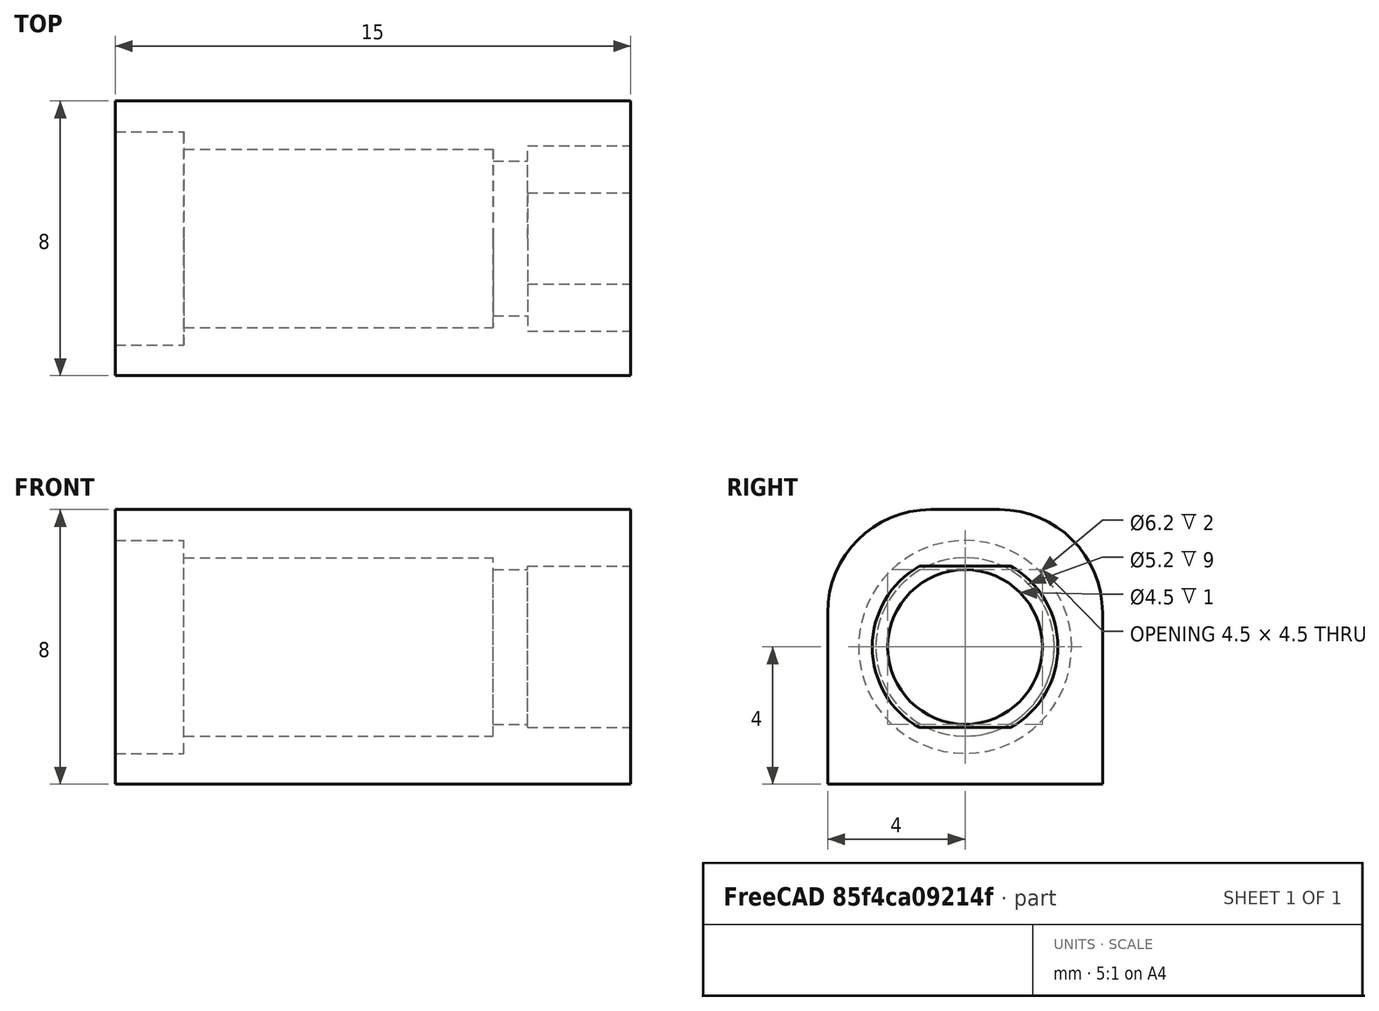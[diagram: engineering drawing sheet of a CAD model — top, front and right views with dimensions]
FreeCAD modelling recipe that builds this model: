
FCSTD DOCUMENT  (FreeCAD 0.14R3700 (Git))
Label: Vactrol_20150326
License: CC-BY 3.0
LicenseURL: http://creativecommons.org/licenses/by/3.0/
objects: Part::Fuse×5, Part::Cylinder×4, Part::Fillet×2, Part::Box×2, Part::Cut×1
note: 14 computed .brp shape members not serialized (recipe doc carries the construction recipe); baked Part::Feature solids carry a one-line shape summary decoded from their .brp

FEATURE [Part::Fillet] Fillet
  Edges = 1 edges r=3: [Edge10]
FEATURE [Part::Fillet] Fillet001  label="housing"
  Base = -> Fillet
  Edges = 1 edges r=3: [Edge13]
  Placement = pos=(0,-4,-4) rot=(0,0,1;0rad)
FEATURE [Part::Cylinder] Cylinder  label="main_bore"
  Angle = 360
  Height = 15
  Placement = pos=(0,0,0) rot=(0,1,0;1.5708rad)
  Radius = 2.25
FEATURE [Part::Cylinder] Cylinder001  label="LED_tip_bore"
  Angle = 360
  Height = 11
  Placement = pos=(0,0,0) rot=(0,1,0;1.5708rad)
  Radius = 2.6
FEATURE [Part::Cylinder] Cylinder002  label="LED_rim_bore"
  Angle = 360
  Height = 2
  Placement = pos=(0,0,0) rot=(0,1,0;1.5708rad)
  Radius = 3.1
FEATURE [Part::Cylinder] Cylinder003  label="LDR_bore"
  Angle = 360
  Height = 3
  Placement = pos=(12,0,0) rot=(0,1,0;1.5708rad)
  Radius = 2.7
FEATURE [Part::Fuse] Fusion  label="LED_bore"
  Base = -> Cylinder001
  Tool = -> Cylinder002
FEATURE [Part::Fuse] Fusion001  label="component_bores"
  Base = -> Cylinder003
  Tool = -> Fusion
FEATURE [Part::Fuse] Fusion002  label="bores"
  Base = -> Cylinder
  Tool = -> Fusion001
FEATURE [Part::Cut] Cut
  Base = -> Fillet001
  Tool = -> Fusion002
FEATURE [Part::Box] Box  label="LDR_guide_bottom"
  Height = 1.65
  Length = 3.5
  Placement = pos=(11.5,-4,-4) rot=(0,0,1;0rad)
  Width = 8
FEATURE [Part::Box] Box001  label="LDR_guide_top"
  Height = 0.45
  Length = 3.5
  Placement = pos=(11.5,-3,2.35) rot=(0,0,1;0rad)
  Width = 6
FEATURE [Part::Fuse] Fusion003  label="LDR_guides"
  Base = -> Box
  Tool = -> Box001
FEATURE [Part::Fuse] Fusion004
  Base = -> Cut
  Tool = -> Fusion003
